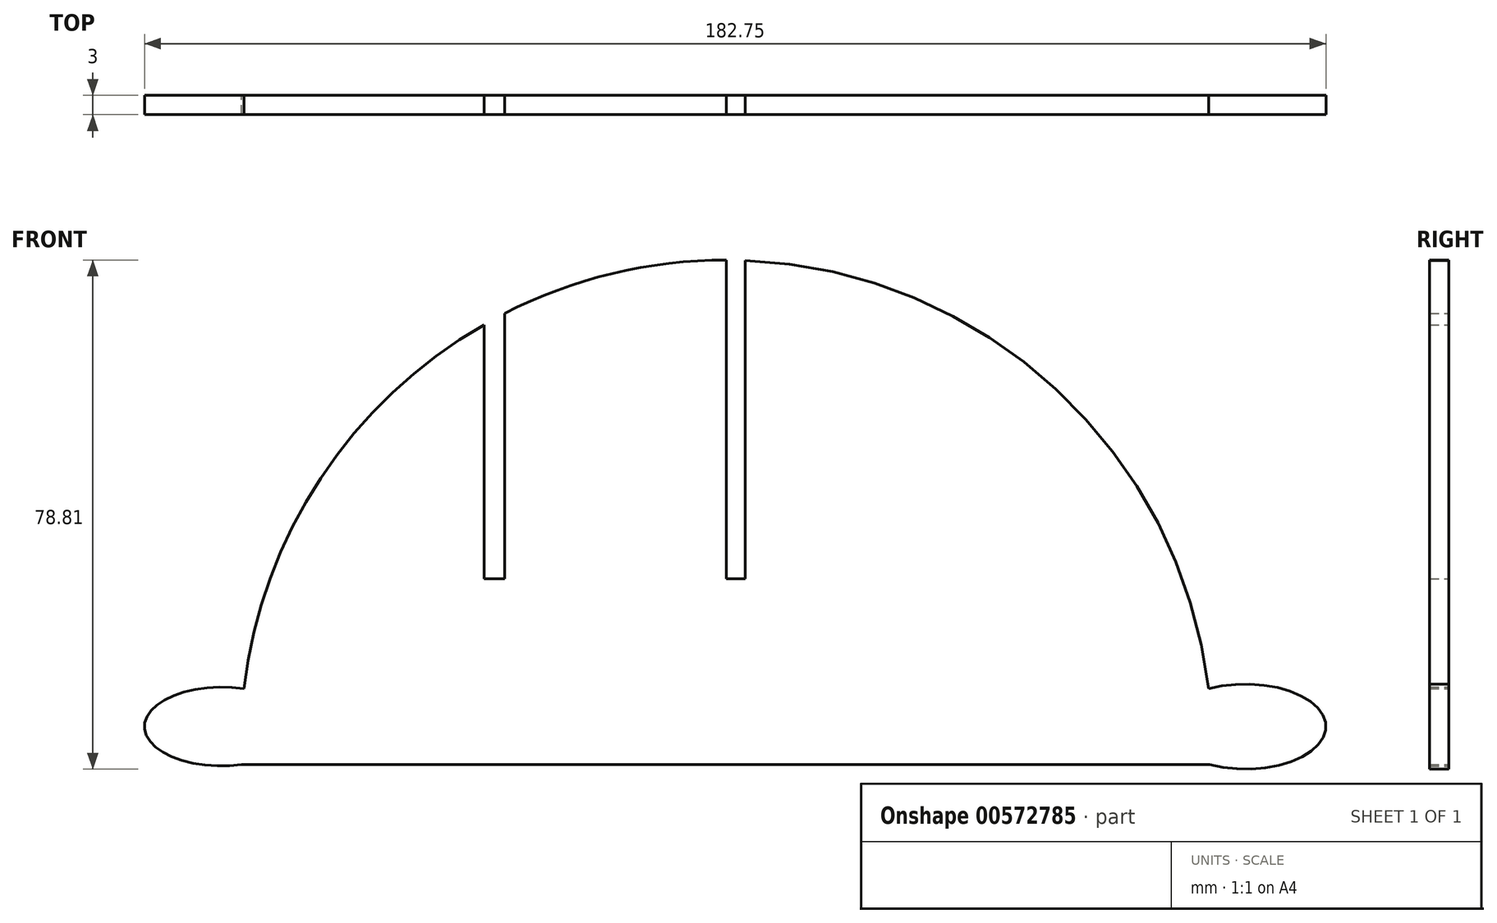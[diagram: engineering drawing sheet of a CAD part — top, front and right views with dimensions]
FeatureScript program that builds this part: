
annotation { "Feature Type Name" : "Feature", "Feature Type Description" : "" }
export const myFeature = defineFeature(function(context is Context, id is Id, definition is map)
    precondition{}
    {
        {
            var Q0;
            Q0=qCreatedBy(makeId("Front.planeOp"),FACE);
            var sketch = newSketch(context, id + "F0", { "sketchPlane" : qUnion([Q0])});
            skLineSegment(sketch, "E0", {"start": v(69.3, 0) * mm, "end": v(-80.7, 0) * mm});
            skArc(sketch, "E1.trimOffspring", {"start": v(68.84, 10.68) * mm, "mid": v(68.79, 11.2) * mm, "end": v(68.73, 11.71) * mm});
            skLineSegment(sketch, "E2", {"start": v(34.97, 28.75) * mm, "end": v(31.77, 28.75) * mm});
            skPoint(sketch, "E3.end.orphan", {"position": v(41.88, 28.75) * mm});
            skPoint(sketch, "E4.start.orphan", {"position": v(31.77, 67.94) * mm});
            skLineSegment(sketch, "E5", {"start": v(-2.8, 28.75) * mm, "end": v(-5.73, 28.75) * mm});
            skLineSegment(sketch, "E6", {"start": v(-40.03, 28.75) * mm, "end": v(-43.23, 28.75) * mm});
            skPoint(sketch, "E7.orphan", {"position": v(64.68, 28.75) * mm});
            skEllipticalArc(sketch, "E8", {});
            skPoint(sketch, "E9.orphan", {"position": v(-80.82, 0) * mm});
            skEllipticalArc(sketch, "E10", {});
            skArc(sketch, "E11.trimOffspring", {"start": v(68.85, 11.74) * mm, "mid": v(58, 42.73) * mm, "end": v(34.97, 66.13) * mm});
            skLineSegment(sketch, "E12", {"start": v(-40.03, 28.75) * mm, "end": v(-40.03, 69.85) * mm});
            skLineSegment(sketch, "E13", {"start": v(-43.23, 28.75) * mm, "end": v(-43.23, 68.11) * mm});
            skArc(sketch, "E14.trimOffspring", {"start": v(-43.23, 68.11) * mm, "mid": v(-68.8, 43.86) * mm, "end": v(-80.5, 10.62) * mm});
            skLineSegment(sketch, "E15", {"start": v(-2.8, 28.75) * mm, "end": v(-2.8, 78.07) * mm});
            skLineSegment(sketch, "E16", {"start": v(-5.73, 28.75) * mm, "end": v(-5.73, 78.13) * mm});
            skArc(sketch, "E17.trimOffspring", {"start": v(-5.73, 78.13) * mm, "mid": v(-23.38, 76.03) * mm, "end": v(-40.03, 69.85) * mm});
            skLineSegment(sketch, "E18", {"start": v(34.97, 28.75) * mm, "end": v(34.97, 66.13) * mm});
            skArc(sketch, "E19", {"start": v(69.3, 0) * mm, "mid": v(60.9, 37.62) * mm, "end": v(34.97, 66.13) * mm});
            skLineSegment(sketch, "E20", {"start": v(31.77, 67.94) * mm, "end": v(31.77, 28.75) * mm});
            skArc(sketch, "E21", {"start": v(69.3, 0) * mm, "mid": v(49.42, 53.97) * mm, "end": v(-2.8, 78.07) * mm});
            const initialGuessF0  = {"E8": [0.0745469480752945, 0.005894604604691267, 1, 0, 0.012467116117477417, 0.006575280191314619, 4.253351988137473, 2.056206815545136], "E10": [-0.08384214341640472, 0.005894604604691267, 1, 0, 0.011900432407855988, 0.006111084969047646, 1.2750591683167358, 4.979354728818344]};
            skSetInitialGuess(sketch, initialGuessF0);
            skSolve(sketch);
        }
        {
            var Q0;
            Q0=qSketchRegion(id+"F0",true);
            extrude(context, id + "F1", {"entities" : qUnion([Q0]), "depth" : 3 * mm, "offsetDistance" : 25 * mm});
        }
    });
